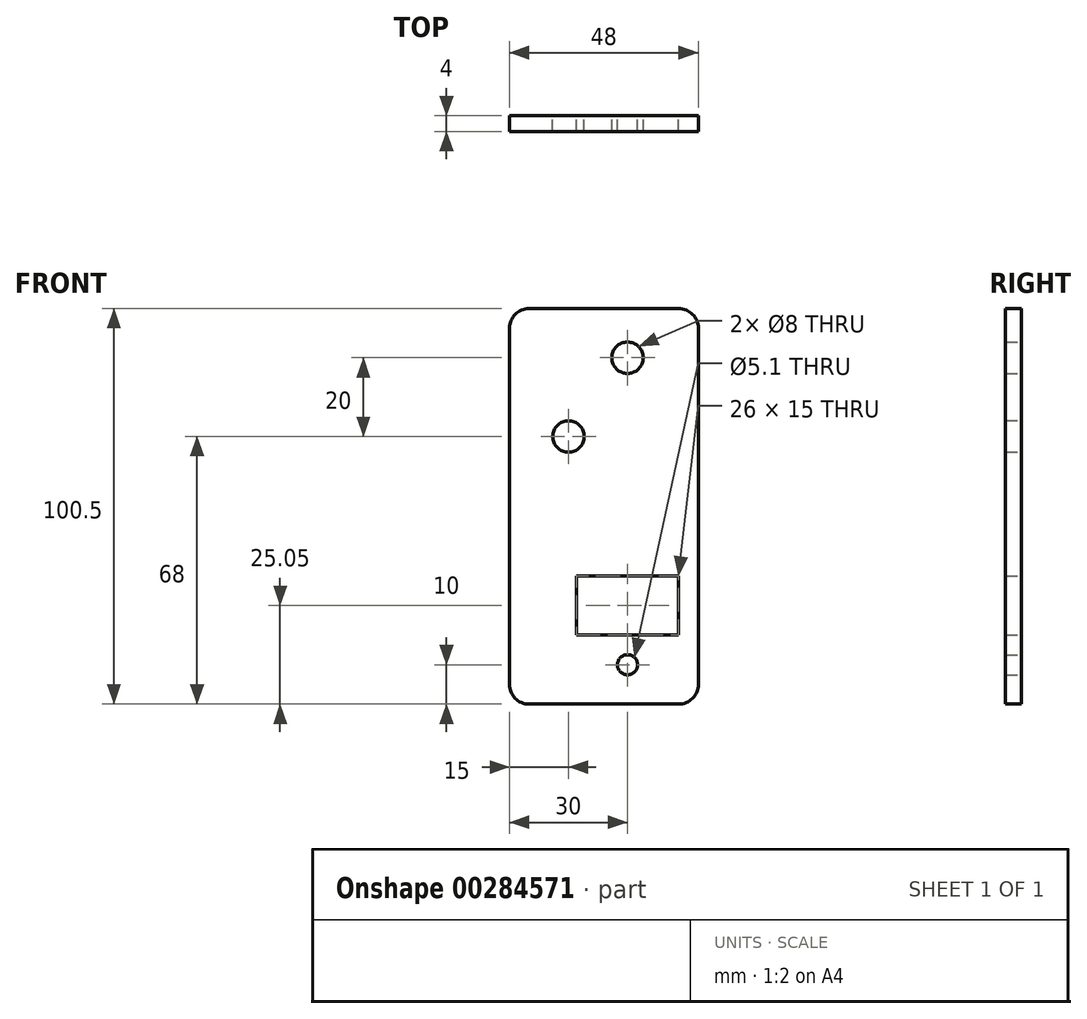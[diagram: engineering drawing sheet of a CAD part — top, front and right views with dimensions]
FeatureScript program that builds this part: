
annotation { "Feature Type Name" : "Feature", "Feature Type Description" : "" }
export const myFeature = defineFeature(function(context is Context, id is Id, definition is map)
    precondition{}
    {
        {
            var Q0;
            Q0=qCreatedBy(makeId("Front.planeOp"),FACE);
            var sketch = newSketch(context, id + "F0", { "sketchPlane" : qUnion([Q0])});
            skLineSegment(sketch, "E0", {"start": v(-17.5, 5) * mm, "end": v(-17.5, 95.5) * mm});
            skLineSegment(sketch, "E1", {"start": v(-12.5, 100.5) * mm, "end": v(25.5, 100.5) * mm});
            skLineSegment(sketch, "E2", {"start": v(30.5, 95.5) * mm, "end": v(30.5, 5) * mm});
            skLineSegment(sketch, "E3", {"start": v(25.5, 0) * mm, "end": v(-12.5, 0) * mm});
            skPoint(sketch, "E4", {"position": v(12.5, 10) * mm});
            skPoint(sketch, "E5", {"position": v(12.5, 88) * mm});
            skPoint(sketch, "E6", {"position": v(-2.5, 68) * mm});
            skPoint(sketch, "E7.visualSharp", {"position": v(-17.5, 100.5) * mm});
            skArc(sketch, "E7.filletArc", {"start": v(-12.5, 100.5) * mm, "mid": v(-16.04, 99.04) * mm, "end": v(-17.5, 95.5) * mm});
            skPoint(sketch, "E8.visualSharp", {"position": v(30.5, 100.5) * mm});
            skArc(sketch, "E8.filletArc", {"start": v(30.5, 95.5) * mm, "mid": v(29.04, 99.04) * mm, "end": v(25.5, 100.5) * mm});
            skPoint(sketch, "E9.visualSharp", {"position": v(0, 0) * mm});
            skPoint(sketch, "E10.visualSharp", {"position": v(30.5, 0) * mm});
            skArc(sketch, "E10.filletArc", {"start": v(25.5, 0) * mm, "mid": v(29.04, 1.46) * mm, "end": v(30.5, 5) * mm});
            skCircle(sketch, "E11", {"center": v(12.5, 10) * mm, "radius": 15 * mm, "construction": true});
            skLineSegment(sketch, "E12.bottom", {"start": v(-0.5, 32.55) * mm, "end": v(25.5, 32.55) * mm});
            skLineSegment(sketch, "E12.top", {"start": v(-0.5, 17.55) * mm, "end": v(25.5, 17.55) * mm});
            skLineSegment(sketch, "E12.left", {"start": v(-0.5, 32.55) * mm, "end": v(-0.5, 17.55) * mm});
            skLineSegment(sketch, "E12.right", {"start": v(25.5, 32.55) * mm, "end": v(25.5, 17.55) * mm});
            skCircle(sketch, "E13", {"center": v(12.5, 10) * mm, "radius": 2.55 * mm});
            skLineSegment(sketch, "E14", {"start": v(12.5, 2.98) * mm, "end": v(12.5, 25) * mm, "construction": true});
            skLineSegment(sketch, "E15", {"start": v(7.5, 24.14) * mm, "end": v(7.5, 4.2) * mm, "construction": true});
            skLineSegment(sketch, "E16", {"start": v(17.5, 24.14) * mm, "end": v(17.5, 2.98) * mm, "construction": true});
            skPoint(sketch, "E17.orphan", {"position": v(12.5, 25.52) * mm});
            skPoint(sketch, "E18.orphan", {"position": v(17.5, 25.52) * mm});
            skCircle(sketch, "E19", {"center": v(7.5, 24.14) * mm, "radius": 3.75 * mm, "construction": true});
            skCircle(sketch, "E20", {"center": v(17.5, 24.14) * mm, "radius": 3.75 * mm, "construction": true});
            skPoint(sketch, "E21.visualSharp", {"position": v(-17.5, 0) * mm});
            skArc(sketch, "E21.filletArc", {"start": v(-17.5, 5) * mm, "mid": v(-16.04, 1.46) * mm, "end": v(-12.5, 0) * mm});
            skCircle(sketch, "E22", {"center": v(-2.5, 68) * mm, "radius": 4 * mm});
            skCircle(sketch, "E23", {"center": v(12.5, 88) * mm, "radius": 4 * mm});
            skSolve(sketch);
        }
        {
            var Q0;
            Q0=qSketchRegion(id+"F0",true);
            extrude(context, id + "F1", {"entities" : qUnion([Q0]), "depth" : 4 * mm});
        }
    });
